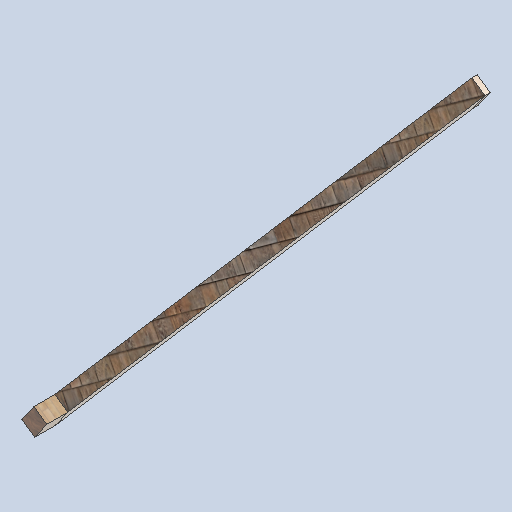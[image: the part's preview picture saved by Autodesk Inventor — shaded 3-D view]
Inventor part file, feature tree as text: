
AUTODESK INVENTOR PART (.ipt)
format: ipt  version: 2024.2 (Build 282272000, 272)  size: 142,336 bytes
history: native  units: in
note: dims shown in document units (in); Inventor stores cm internally (conversion verified against a paired STEP export)
features: sketch x4, other x3, plane x2
ambient origin geometry x8: Origin, YZ Plane, XZ Plane, XY Plane, X Axis, Y Axis, Z Axis, Center Point
bodies: Solid1 (feature_tree)
feature tree (9):
  other  "support_beam_segment_0102.ipt"
  other  "Solid1::support_beam_segment_0102.ipt"
  other  "TaggingFeature1"
  sketch  "Sketch1"  dims[d0=0.3937in]
  sketch  "Sketch2"
  sketch  "Sketch3"
  sketch  "Sketch4"
  plane  "Work Plane1"
  plane  "Work Plane2"
